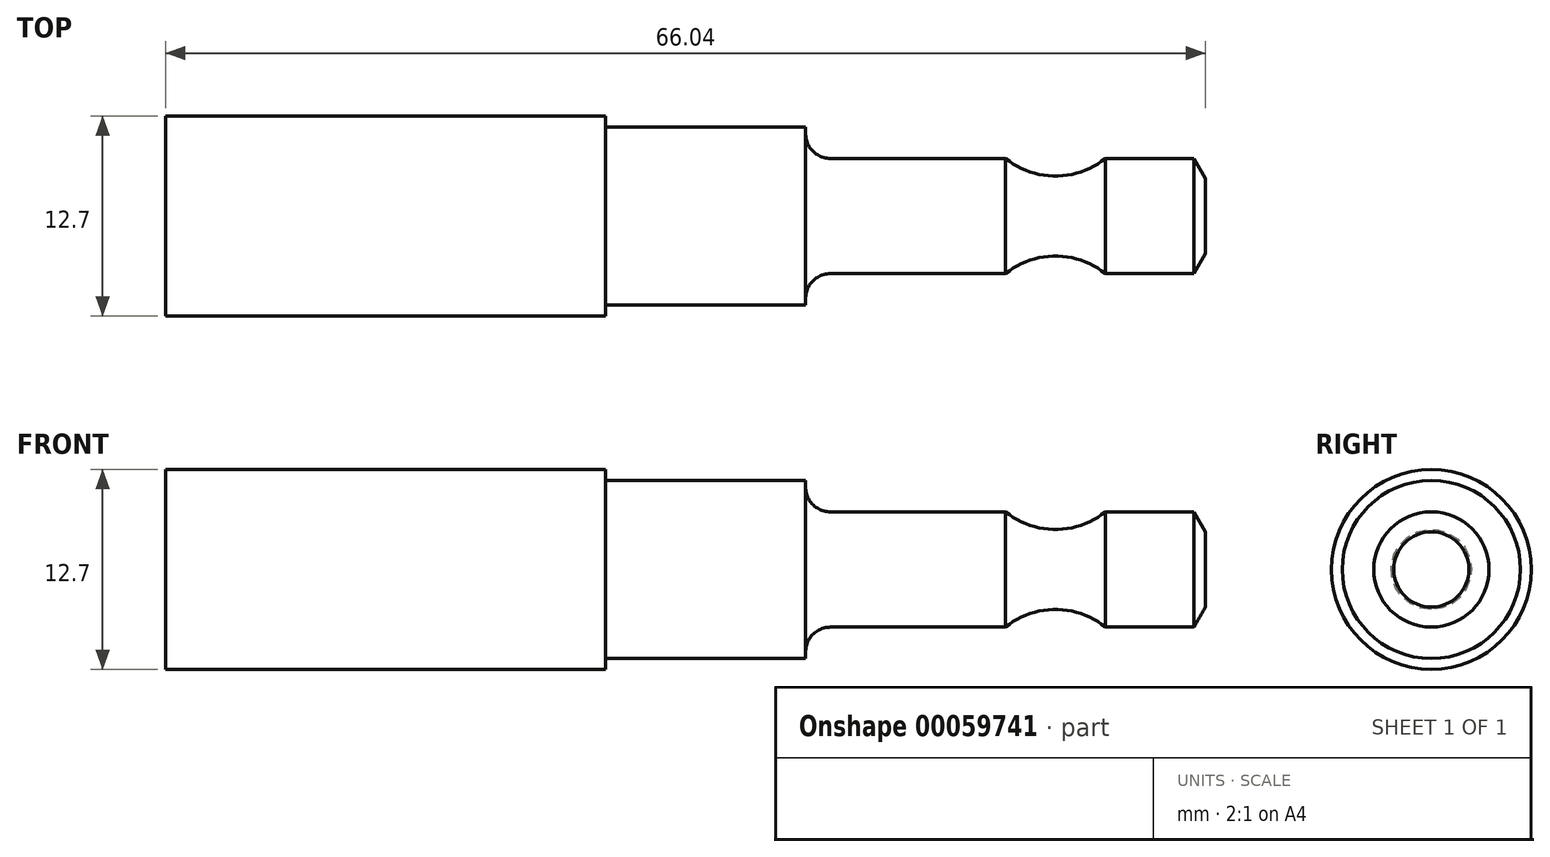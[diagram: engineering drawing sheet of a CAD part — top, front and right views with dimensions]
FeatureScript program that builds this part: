
annotation { "Feature Type Name" : "Feature", "Feature Type Description" : "" }
export const myFeature = defineFeature(function(context is Context, id is Id, definition is map)
    precondition{}
    {
        {
            var Q0;
            Q0=qCreatedBy(makeId("Front.planeOp"),FACE);
            var sketch = newSketch(context, id + "F0", { "sketchPlane" : qUnion([Q0])});
            skLineSegment(sketch, "E0", {"start": v(-0.73, 3.66) * mm, "end": v(-6.35, 3.66) * mm});
            skLineSegment(sketch, "E1", {"start": v(0, 0) * mm, "end": v(0, 3.66) * mm, "construction": true});
            skLineSegment(sketch, "E2", {"start": v(-12.7, 3.66) * mm, "end": v(-23.81, 3.66) * mm});
            skArc(sketch, "E3", {"start": v(-12.7, 3.66) * mm, "mid": v(-9.53, 2.54) * mm, "end": v(-6.35, 3.66) * mm});
            skLineSegment(sketch, "E4", {"start": v(0, 0) * mm, "end": v(-38.1, 0) * mm});
            skLineSegment(sketch, "E5", {"start": v(-0.73, 3.66) * mm, "end": v(0, 2.4) * mm});
            skLineSegment(sketch, "E6", {"start": v(0, 2.4) * mm, "end": v(0, 0) * mm});
            skLineSegment(sketch, "E7", {"start": v(-25.4, 5.25) * mm, "end": v(-25.4, 5.66) * mm});
            skLineSegment(sketch, "E8", {"start": v(-25.4, 5.66) * mm, "end": v(-38.1, 5.66) * mm});
            skLineSegment(sketch, "E9", {"start": v(-38.1, 5.66) * mm, "end": v(-38.1, 0) * mm});
            skPoint(sketch, "E10.visualSharp", {"position": v(-25.4, 3.66) * mm});
            skArc(sketch, "E10.filletArc", {"start": v(-25.4, 5.25) * mm, "mid": v(-24.94, 4.13) * mm, "end": v(-23.81, 3.66) * mm});
            skLineSegment(sketch, "E11", {"start": v(-38.1, 0) * mm, "end": v(0, 0) * mm});
            skSolve(sketch);
        }
        {
            var Q0;
            Q0=qSketchRegion(id+"F0",true);
            var Q1;
            Q1=qBodyType(qCreatedBy(id+"F0",EDGE),BodyType.WIRE);
            var Q2;
            Q2=sQuery(id+"F0.wireOp",EDGE,"E4");
            revolve(context, id + "F1", {"entities" : qUnion([Q0]), "surfaceEntities" : qUnion([Q1]), "axis" : qUnion([Q2]), "revolveType" : RevolveType.FULL});
        }
        {
            var Q0;
            Q0=makeQuery(id+"F1.opRevolve","SWEPT_FACE",FACE,{"disambiguationData":[OSD([sQuery(id+"F0.wireOp",EDGE,"E9")])]});
            var sketch = newSketch(context, id + "F2", { "sketchPlane" : qUnion([Q0])});
            skCircle(sketch, "E12", {"center": v(0, 0) * mm, "radius": 6.35 * mm});
            skSolve(sketch);
        }
        {
            var Q0;
            Q0=qSketchRegion(id+"F2",true);
            extrude(context, id + "F3", {"entities" : qUnion([Q0]), "depth" : 27.94 * mm});
        }
    });
